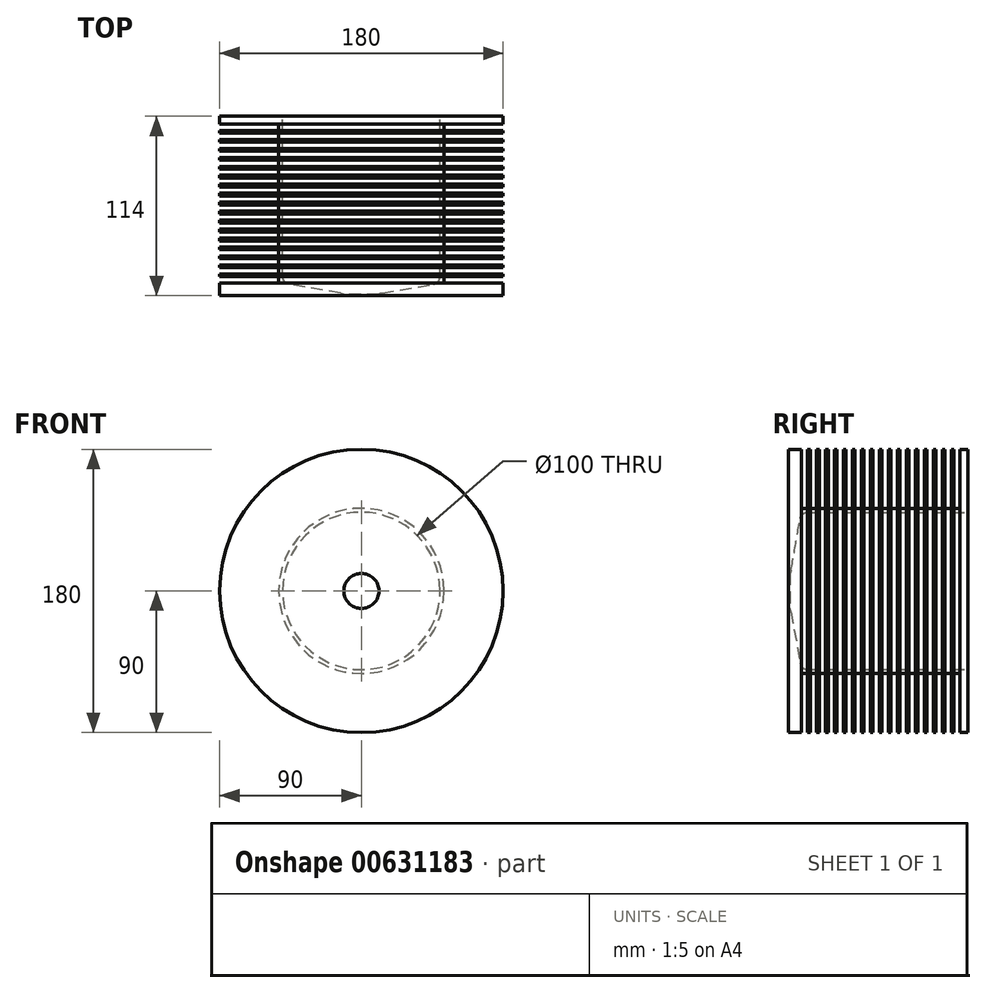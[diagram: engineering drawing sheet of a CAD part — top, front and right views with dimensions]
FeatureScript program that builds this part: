
annotation { "Feature Type Name" : "Feature", "Feature Type Description" : "" }
export const myFeature = defineFeature(function(context is Context, id is Id, definition is map)
    precondition{}
    {
        {
            var Q0;
            Q0=qCreatedBy(makeId("Right.planeOp"),FACE);
            var sketch = newSketch(context, id + "F0", { "sketchPlane" : qUnion([Q0])});
            skLineSegment(sketch, "E0", {"start": v(-114, 90) * mm, "end": v(-114, 50) * mm});
            skLineSegment(sketch, "E1", {"start": v(-101.7, 50) * mm, "end": v(0, 50) * mm});
            skLineSegment(sketch, "E2", {"start": v(0, 50) * mm, "end": v(0, 90) * mm});
            skLineSegment(sketch, "E3", {"start": v(-114, 90) * mm, "end": v(-105.9, 90) * mm});
            skLineSegment(sketch, "E4", {"start": v(-105.9, 90) * mm, "end": v(-105.9, 52.5) * mm});
            skLineSegment(sketch, "E5", {"start": v(-105.9, 52.5) * mm, "end": v(-101.9, 52.5) * mm});
            skLineSegment(sketch, "E6", {"start": v(-101.9, 52.5) * mm, "end": v(-101.9, 90) * mm});
            skLineSegment(sketch, "E7", {"start": v(-101.9, 90) * mm, "end": v(-100.2, 90) * mm});
            skLineSegment(sketch, "E8", {"start": v(-100.2, 90) * mm, "end": v(-100.2, 52.5) * mm});
            skLineSegment(sketch, "E9.1.0.0", {"start": v(-100.2, 52.5) * mm, "end": v(-96.2, 52.5) * mm});
            skLineSegment(sketch, "E9.1.0.1", {"start": v(-94.5, 90) * mm, "end": v(-94.5, 52.5) * mm});
            skLineSegment(sketch, "E9.1.0.2", {"start": v(-96.2, 52.5) * mm, "end": v(-96.2, 90) * mm});
            skLineSegment(sketch, "E9.1.0.3", {"start": v(-96.2, 90) * mm, "end": v(-94.5, 90) * mm});
            skLineSegment(sketch, "E9.2.0.0", {"start": v(-94.5, 52.5) * mm, "end": v(-90.5, 52.5) * mm});
            skLineSegment(sketch, "E9.2.0.1", {"start": v(-88.8, 90) * mm, "end": v(-88.8, 52.5) * mm});
            skLineSegment(sketch, "E9.2.0.2", {"start": v(-90.5, 52.5) * mm, "end": v(-90.5, 90) * mm});
            skLineSegment(sketch, "E9.2.0.3", {"start": v(-90.5, 90) * mm, "end": v(-88.8, 90) * mm});
            skLineSegment(sketch, "E9.3.0.0", {"start": v(-88.8, 52.5) * mm, "end": v(-84.8, 52.5) * mm});
            skLineSegment(sketch, "E9.3.0.1", {"start": v(-83.1, 90) * mm, "end": v(-83.1, 52.5) * mm});
            skLineSegment(sketch, "E9.3.0.2", {"start": v(-84.8, 52.5) * mm, "end": v(-84.8, 90) * mm});
            skLineSegment(sketch, "E9.3.0.3", {"start": v(-84.8, 90) * mm, "end": v(-83.1, 90) * mm});
            skLineSegment(sketch, "E9.4.0.0", {"start": v(-83.1, 52.5) * mm, "end": v(-79.1, 52.5) * mm});
            skLineSegment(sketch, "E9.4.0.1", {"start": v(-77.4, 90) * mm, "end": v(-77.4, 52.5) * mm});
            skLineSegment(sketch, "E9.4.0.2", {"start": v(-79.1, 52.5) * mm, "end": v(-79.1, 90) * mm});
            skLineSegment(sketch, "E9.4.0.3", {"start": v(-79.1, 90) * mm, "end": v(-77.4, 90) * mm});
            skLineSegment(sketch, "E9.5.0.0", {"start": v(-77.4, 52.5) * mm, "end": v(-73.4, 52.5) * mm});
            skLineSegment(sketch, "E9.5.0.1", {"start": v(-71.7, 90) * mm, "end": v(-71.7, 52.5) * mm});
            skLineSegment(sketch, "E9.5.0.2", {"start": v(-73.4, 52.5) * mm, "end": v(-73.4, 90) * mm});
            skLineSegment(sketch, "E9.5.0.3", {"start": v(-73.4, 90) * mm, "end": v(-71.7, 90) * mm});
            skLineSegment(sketch, "E9.6.0.0", {"start": v(-71.7, 52.5) * mm, "end": v(-67.7, 52.5) * mm});
            skLineSegment(sketch, "E9.6.0.1", {"start": v(-66, 90) * mm, "end": v(-66, 52.5) * mm});
            skLineSegment(sketch, "E9.6.0.2", {"start": v(-67.7, 52.5) * mm, "end": v(-67.7, 90) * mm});
            skLineSegment(sketch, "E9.6.0.3", {"start": v(-67.7, 90) * mm, "end": v(-66, 90) * mm});
            skLineSegment(sketch, "E9.7.0.0", {"start": v(-66, 52.5) * mm, "end": v(-62, 52.5) * mm});
            skLineSegment(sketch, "E9.7.0.1", {"start": v(-60.3, 90) * mm, "end": v(-60.3, 52.5) * mm});
            skLineSegment(sketch, "E9.7.0.2", {"start": v(-62, 52.5) * mm, "end": v(-62, 90) * mm});
            skLineSegment(sketch, "E9.7.0.3", {"start": v(-62, 90) * mm, "end": v(-60.3, 90) * mm});
            skLineSegment(sketch, "E9.8.0.0", {"start": v(-60.3, 52.5) * mm, "end": v(-56.3, 52.5) * mm});
            skLineSegment(sketch, "E9.8.0.1", {"start": v(-54.6, 90) * mm, "end": v(-54.6, 52.5) * mm});
            skLineSegment(sketch, "E9.8.0.2", {"start": v(-56.3, 52.5) * mm, "end": v(-56.3, 90) * mm});
            skLineSegment(sketch, "E9.8.0.3", {"start": v(-56.3, 90) * mm, "end": v(-54.6, 90) * mm});
            skLineSegment(sketch, "E9.9.0.0", {"start": v(-54.6, 52.5) * mm, "end": v(-50.6, 52.5) * mm});
            skLineSegment(sketch, "E9.9.0.1", {"start": v(-48.9, 90) * mm, "end": v(-48.9, 52.5) * mm});
            skLineSegment(sketch, "E9.9.0.2", {"start": v(-50.6, 52.5) * mm, "end": v(-50.6, 90) * mm});
            skLineSegment(sketch, "E9.9.0.3", {"start": v(-50.6, 90) * mm, "end": v(-48.9, 90) * mm});
            skLineSegment(sketch, "E9.10.0.0", {"start": v(-48.9, 52.5) * mm, "end": v(-44.9, 52.5) * mm});
            skLineSegment(sketch, "E9.10.0.1", {"start": v(-43.2, 90) * mm, "end": v(-43.2, 52.5) * mm});
            skLineSegment(sketch, "E9.10.0.2", {"start": v(-44.9, 52.5) * mm, "end": v(-44.9, 90) * mm});
            skLineSegment(sketch, "E9.10.0.3", {"start": v(-44.9, 90) * mm, "end": v(-43.2, 90) * mm});
            skLineSegment(sketch, "E9.11.0.0", {"start": v(-43.2, 52.5) * mm, "end": v(-39.2, 52.5) * mm});
            skLineSegment(sketch, "E9.11.0.1", {"start": v(-37.5, 90) * mm, "end": v(-37.5, 52.5) * mm});
            skLineSegment(sketch, "E9.11.0.2", {"start": v(-39.2, 52.5) * mm, "end": v(-39.2, 90) * mm});
            skLineSegment(sketch, "E9.11.0.3", {"start": v(-39.2, 90) * mm, "end": v(-37.5, 90) * mm});
            skLineSegment(sketch, "E9.12.0.0", {"start": v(-37.5, 52.5) * mm, "end": v(-33.5, 52.5) * mm});
            skLineSegment(sketch, "E9.12.0.1", {"start": v(-31.8, 90) * mm, "end": v(-31.8, 52.5) * mm});
            skLineSegment(sketch, "E9.12.0.2", {"start": v(-33.5, 52.5) * mm, "end": v(-33.5, 90) * mm});
            skLineSegment(sketch, "E9.12.0.3", {"start": v(-33.5, 90) * mm, "end": v(-31.8, 90) * mm});
            skLineSegment(sketch, "E9.13.0.0", {"start": v(-31.8, 52.5) * mm, "end": v(-27.8, 52.5) * mm});
            skLineSegment(sketch, "E9.13.0.1", {"start": v(-26.1, 90) * mm, "end": v(-26.1, 52.5) * mm});
            skLineSegment(sketch, "E9.13.0.2", {"start": v(-27.8, 52.5) * mm, "end": v(-27.8, 90) * mm});
            skLineSegment(sketch, "E9.13.0.3", {"start": v(-27.8, 90) * mm, "end": v(-26.1, 90) * mm});
            skLineSegment(sketch, "E9.14.0.0", {"start": v(-26.1, 52.5) * mm, "end": v(-22.1, 52.5) * mm});
            skLineSegment(sketch, "E9.14.0.1", {"start": v(-20.4, 90) * mm, "end": v(-20.4, 52.5) * mm});
            skLineSegment(sketch, "E9.14.0.2", {"start": v(-22.1, 52.5) * mm, "end": v(-22.1, 90) * mm});
            skLineSegment(sketch, "E9.14.0.3", {"start": v(-22.1, 90) * mm, "end": v(-20.4, 90) * mm});
            skLineSegment(sketch, "E9.15.0.0", {"start": v(-20.4, 52.5) * mm, "end": v(-16.4, 52.5) * mm});
            skLineSegment(sketch, "E9.15.0.1", {"start": v(-14.7, 90) * mm, "end": v(-14.7, 52.5) * mm});
            skLineSegment(sketch, "E9.15.0.2", {"start": v(-16.4, 52.5) * mm, "end": v(-16.4, 90) * mm});
            skLineSegment(sketch, "E9.15.0.3", {"start": v(-16.4, 90) * mm, "end": v(-14.7, 90) * mm});
            skLineSegment(sketch, "E9.16.0.0", {"start": v(-14.7, 52.5) * mm, "end": v(-10.7, 52.5) * mm});
            skLineSegment(sketch, "E9.16.0.1", {"start": v(-9, 90) * mm, "end": v(-9, 52.5) * mm});
            skLineSegment(sketch, "E9.16.0.2", {"start": v(-10.7, 52.5) * mm, "end": v(-10.7, 90) * mm});
            skLineSegment(sketch, "E9.16.0.3", {"start": v(-10.7, 90) * mm, "end": v(-9, 90) * mm});
            skLineSegment(sketch, "E9.direction1", {"start": v(-105.9, 52.5) * mm, "end": v(-100.2, 52.5) * mm, "construction": true});
            skLineSegment(sketch, "E10", {"start": v(-9, 52.5) * mm, "end": v(-5, 52.5) * mm});
            skLineSegment(sketch, "E11", {"start": v(-5, 52.5) * mm, "end": v(-5, 90) * mm});
            skLineSegment(sketch, "E12", {"start": v(-5, 90) * mm, "end": v(0, 90) * mm});
            skLineSegment(sketch, "E13", {"start": v(0, 0) * mm, "end": v(-12.9, 0) * mm, "construction": true});
            skLineSegment(sketch, "E14", {"start": v(-106.63, 45.87) * mm, "end": v(-112.4, 13.18) * mm});
            skLineSegment(sketch, "E15", {"start": v(-112.36, 11.38) * mm, "end": v(-114.44, 9.63) * mm});
            skLineSegment(sketch, "E16", {"start": v(-114, 12.14) * mm, "end": v(-114, 50) * mm});
            skPoint(sketch, "E17.newPointA", {"position": v(-105.9, 50) * mm});
            skArc(sketch, "E17.filletArc", {"start": v(-101.7, 50) * mm, "mid": v(-104.92, 48.83) * mm, "end": v(-106.63, 45.87) * mm});
            skPoint(sketch, "E18.visualSharp", {"position": v(-112.77, 11.03) * mm});
            skArc(sketch, "E18.filletArc", {"start": v(-114.44, 9.63) * mm, "mid": v(-113.1, 11.22) * mm, "end": v(-112.4, 13.18) * mm});
            skPoint(sketch, "E19.visualSharp", {"position": v(-114, 10) * mm});
            skArc(sketch, "E19.filletArc", {"start": v(-114, 12.14) * mm, "mid": v(-113.42, 11.24) * mm, "end": v(-112.36, 11.38) * mm});
            skSolve(sketch);
        }
        {
            var Q0;
            Q0=makeQuery(id+"F0.imprint","IMPRINT",FACE,{"disambiguationData":[TD([[makeQuery(id+"F0.imprint","IMPRINT",EDGE,{"derivedFrom":sQuery(id+"F0.wireOp",EDGE,"E0")}),1.0]])]});
            var Q1;
            Q1=sQuery(id+"F0.wireOp",EDGE,"E13");
            revolve(context, id + "F1", {"entities" : qUnion([Q0]), "axis" : qUnion([Q1]), "revolveType" : RevolveType.FULL});
        }
    });
